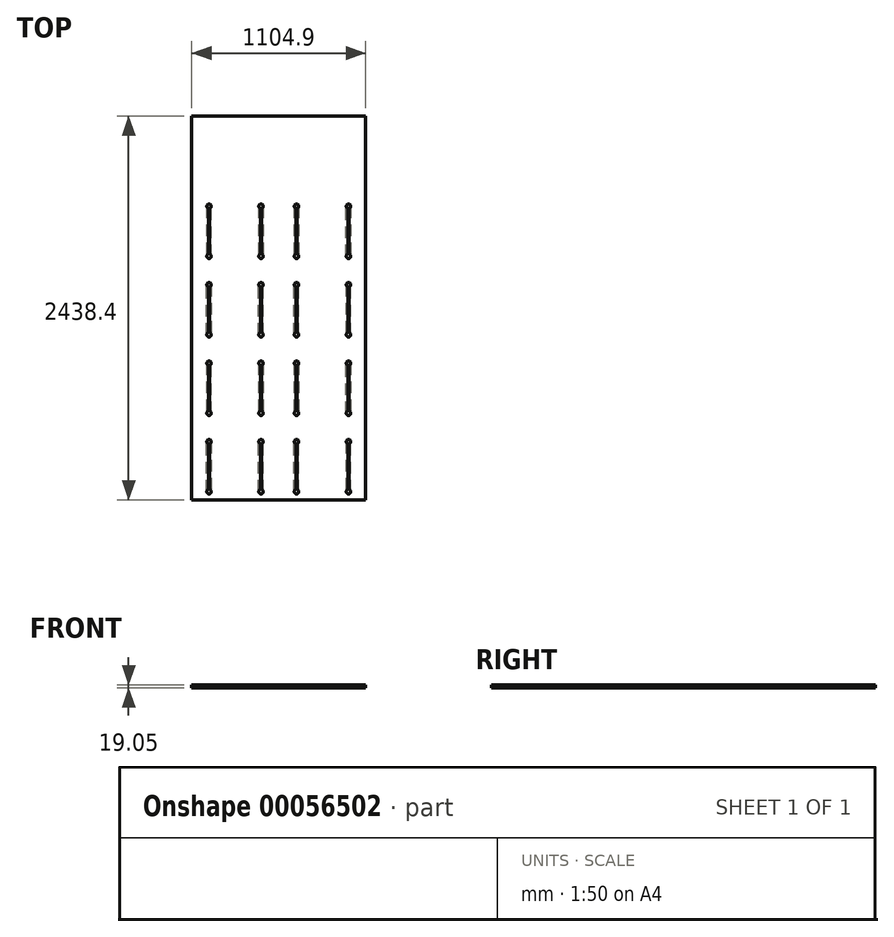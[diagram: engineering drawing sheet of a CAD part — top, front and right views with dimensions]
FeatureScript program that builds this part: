
annotation { "Feature Type Name" : "Feature", "Feature Type Description" : "" }
export const myFeature = defineFeature(function(context is Context, id is Id, definition is map)
    precondition{}
    {
        {
            var Q0;
            Q0=qCreatedBy(makeId("Top.planeOp"),FACE);
            var sketch = newSketch(context, id + "F0", { "sketchPlane" : qUnion([Q0])});
            skLineSegment(sketch, "E0", {"start": v(0, 0) * mm, "end": v(1219.2, 0) * mm, "construction": true});
            skLineSegment(sketch, "E1", {"start": v(1219.2, 0) * mm, "end": v(1219.2, 2438.4) * mm, "construction": true});
            skLineSegment(sketch, "E2", {"start": v(0, 2438.4) * mm, "end": v(1219.2, 2438.4) * mm, "construction": true});
            skLineSegment(sketch, "E3", {"start": v(0, 0) * mm, "end": v(0, 2438.4) * mm, "construction": true});
            skLineSegment(sketch, "E4", {"start": v(609.6, 2700.6) * mm, "end": v(609.6, -302.24) * mm, "construction": true});
            skPoint(sketch, "E4.startSnap0", {"position": v(609.6, 2438.4) * mm});
            skLineSegment(sketch, "E5.bottom", {"start": v(57.15, 0) * mm, "end": v(1162.05, 0) * mm});
            skLineSegment(sketch, "E5.top", {"start": v(57.15, 2438.4) * mm, "end": v(1162.05, 2438.4) * mm});
            skLineSegment(sketch, "E5.left", {"start": v(57.15, 0) * mm, "end": v(57.15, 2438.4) * mm});
            skLineSegment(sketch, "E5.right", {"start": v(1162.05, 0) * mm, "end": v(1162.05, 2438.4) * mm});
            skLineSegment(sketch, "E6.bottom", {"start": v(50.8, 0) * mm, "end": v(88.9, 0) * mm, "construction": true});
            skLineSegment(sketch, "E6.left", {"start": v(50.8, 0) * mm, "end": v(50.8, 2438.4) * mm, "construction": true});
            skLineSegment(sketch, "E6.right", {"start": v(88.9, 0) * mm, "end": v(88.9, 2438.4) * mm, "construction": true});
            skLineSegment(sketch, "E7.bottom", {"start": v(1168.4, 0) * mm, "end": v(1130.3, 0) * mm, "construction": true});
            skLineSegment(sketch, "E7.top", {"start": v(1168.4, 2438.4) * mm, "end": v(1130.3, 2438.4) * mm, "construction": true});
            skLineSegment(sketch, "E7.left", {"start": v(1168.4, 0) * mm, "end": v(1168.4, 2438.4) * mm, "construction": true});
            skLineSegment(sketch, "E7.right", {"start": v(1130.3, 0) * mm, "end": v(1130.3, 2438.4) * mm, "construction": true});
            skLineSegment(sketch, "E8.bottom", {"start": v(88.9, 38.1) * mm, "end": v(1130.3, 38.1) * mm, "construction": true});
            skLineSegment(sketch, "E8.left", {"start": v(88.9, 38.1) * mm, "end": v(88.9, 0) * mm, "construction": true});
            skLineSegment(sketch, "E8.right", {"start": v(1130.3, 38.1) * mm, "end": v(1130.3, 0) * mm, "construction": true});
            skLineSegment(sketch, "E9.bottom", {"start": v(88.9, 2400.3) * mm, "end": v(1130.3, 2400.3) * mm, "construction": true});
            skLineSegment(sketch, "E9.top", {"start": v(88.9, 2438.4) * mm, "end": v(1130.3, 2438.4) * mm, "construction": true});
            skLineSegment(sketch, "E9.left", {"start": v(88.9, 2400.3) * mm, "end": v(88.9, 2438.4) * mm, "construction": true});
            skLineSegment(sketch, "E9.right", {"start": v(1130.3, 2400.3) * mm, "end": v(1130.3, 2438.4) * mm, "construction": true});
            skLineSegment(sketch, "E10", {"start": v(-72.35, 2076.45) * mm, "end": v(1337.6, 2076.45) * mm, "construction": true});
            skLineSegment(sketch, "E11.0.1.0", {"start": v(-72.35, 1733.55) * mm, "end": v(1337.6, 1733.55) * mm, "construction": true});
            skLineSegment(sketch, "E11.0.2.0", {"start": v(-72.35, 1390.65) * mm, "end": v(1337.6, 1390.65) * mm, "construction": true});
            skLineSegment(sketch, "E11.0.3.0", {"start": v(-72.35, 1047.75) * mm, "end": v(1337.6, 1047.75) * mm, "construction": true});
            skLineSegment(sketch, "E11.0.4.0", {"start": v(-72.35, 704.85) * mm, "end": v(1337.6, 704.85) * mm, "construction": true});
            skLineSegment(sketch, "E11.0.5.0", {"start": v(-72.35, 361.95) * mm, "end": v(1337.6, 361.95) * mm, "construction": true});
            skLineSegment(sketch, "E11.direction1", {"start": v(-72.35, 2076.45) * mm, "end": v(-46.95, 2076.45) * mm, "construction": true});
            skLineSegment(sketch, "E11.direction2", {"start": v(-72.35, 2076.45) * mm, "end": v(-72.35, 1733.55) * mm, "construction": true});
            skPoint(sketch, "E12", {"position": v(114.3, 63.5) * mm});
            skPoint(sketch, "E13", {"position": v(609.6, 63.5) * mm});
            skPoint(sketch, "E14.MirrorP", {"position": v(1104.9, 63.5) * mm});
            skPoint(sketch, "E15", {"position": v(361.95, 63.5) * mm});
            skPoint(sketch, "E16", {"position": v(114.3, 279.4) * mm});
            skPoint(sketch, "E17.MirrorP", {"position": v(857.25, 63.5) * mm});
            skPoint(sketch, "E18", {"position": v(361.95, 279.4) * mm});
            skPoint(sketch, "E19", {"position": v(609.6, 279.4) * mm});
            skPoint(sketch, "E20", {"position": v(857.25, 279.4) * mm});
            skPoint(sketch, "E21", {"position": v(1104.9, 279.4) * mm});
            skPoint(sketch, "E22.MirrorP", {"position": v(1104.9, 444.5) * mm});
            skPoint(sketch, "E23.MirrorP", {"position": v(857.25, 444.5) * mm});
            skPoint(sketch, "E24.MirrorP", {"position": v(609.6, 444.5) * mm});
            skPoint(sketch, "E25.MirrorP", {"position": v(361.95, 444.5) * mm});
            skPoint(sketch, "E26.MirrorP", {"position": v(114.3, 444.5) * mm});
            skPoint(sketch, "E27", {"position": v(114.3, 622.3) * mm});
            skPoint(sketch, "E28", {"position": v(361.95, 622.3) * mm});
            skPoint(sketch, "E29", {"position": v(857.25, 622.3) * mm});
            skPoint(sketch, "E30", {"position": v(1104.9, 622.3) * mm});
            skPoint(sketch, "E31", {"position": v(114.3, 965.2) * mm});
            skPoint(sketch, "E32", {"position": v(361.95, 965.2) * mm});
            skPoint(sketch, "E33", {"position": v(857.25, 965.2) * mm});
            skPoint(sketch, "E34", {"position": v(1104.9, 965.2) * mm});
            skPoint(sketch, "E35", {"position": v(609.6, 622.3) * mm});
            skPoint(sketch, "E36.MirrorP", {"position": v(1104.9, 787.4) * mm});
            skPoint(sketch, "E37.MirrorP", {"position": v(857.25, 787.4) * mm});
            skPoint(sketch, "E38.MirrorP", {"position": v(609.6, 787.4) * mm});
            skPoint(sketch, "E39.MirrorP", {"position": v(361.95, 787.4) * mm});
            skPoint(sketch, "E40.MirrorP", {"position": v(114.3, 787.4) * mm});
            skPoint(sketch, "E41", {"position": v(609.6, 965.2) * mm});
            skPoint(sketch, "E42.MirrorP", {"position": v(1104.9, 1130.3) * mm});
            skPoint(sketch, "E43.MirrorP", {"position": v(857.25, 1130.3) * mm});
            skPoint(sketch, "E44.MirrorP", {"position": v(609.6, 1130.3) * mm});
            skPoint(sketch, "E45.MirrorP", {"position": v(361.95, 1130.3) * mm});
            skPoint(sketch, "E46.MirrorP", {"position": v(114.3, 1130.3) * mm});
            skPoint(sketch, "E47.0.1.0", {"position": v(114.3, 1308.1) * mm});
            skPoint(sketch, "E47.0.1.1", {"position": v(361.95, 1308.1) * mm});
            skPoint(sketch, "E47.0.1.2", {"position": v(609.6, 1308.1) * mm});
            skPoint(sketch, "E47.0.1.3", {"position": v(857.25, 1308.1) * mm});
            skPoint(sketch, "E47.0.1.4", {"position": v(1104.9, 1308.1) * mm});
            skPoint(sketch, "E47.0.2.0", {"position": v(114.3, 1651) * mm});
            skPoint(sketch, "E47.0.2.1", {"position": v(361.95, 1651) * mm});
            skPoint(sketch, "E47.0.2.2", {"position": v(609.6, 1651) * mm});
            skPoint(sketch, "E47.0.2.3", {"position": v(857.25, 1651) * mm});
            skPoint(sketch, "E47.0.2.4", {"position": v(1104.9, 1651) * mm});
            skLineSegment(sketch, "E47.direction1", {"start": v(114.3, 965.2) * mm, "end": v(139.7, 965.2) * mm, "construction": true});
            skLineSegment(sketch, "E47.direction2", {"start": v(114.3, 965.2) * mm, "end": v(114.3, 1308.1) * mm, "construction": true});
            skPoint(sketch, "E48.MirrorP", {"position": v(1104.9, 1473.2) * mm});
            skPoint(sketch, "E49.MirrorP", {"position": v(857.25, 1473.2) * mm});
            skPoint(sketch, "E50.MirrorP", {"position": v(609.6, 1473.2) * mm});
            skPoint(sketch, "E51.MirrorP", {"position": v(361.95, 1473.2) * mm});
            skPoint(sketch, "E52.MirrorP", {"position": v(114.3, 1473.2) * mm});
            skPoint(sketch, "E53.MirrorP", {"position": v(1104.9, 1816.1) * mm});
            skPoint(sketch, "E54.MirrorP", {"position": v(857.25, 1816.1) * mm});
            skPoint(sketch, "E55.MirrorP", {"position": v(609.6, 1816.1) * mm});
            skPoint(sketch, "E56.MirrorP", {"position": v(361.95, 1816.1) * mm});
            skPoint(sketch, "E57.MirrorP", {"position": v(114.3, 1816.1) * mm});
            skLineSegment(sketch, "E58", {"start": v(-178.61, 1879.6) * mm, "end": v(1741, 1879.6) * mm, "construction": true});
            skSolve(sketch);
        }
        {
            var Q0;
            Q0 = qSketchRegion(id + "F0", true);
            extrude(context, id + "F1", {"entities" : qUnion([Q0]), "depth" : 19.05 * mm});
        }
        {
            var Q0;
            Q0=qCreatedBy(makeId("Top.planeOp"),FACE);
            var sketch = newSketch(context, id + "F2", { "sketchPlane" : qUnion([Q0])});
            skLineSegment(sketch, "E59.0.0", {"start": v(57.15, 2438.4) * mm, "end": v(57.15, 0) * mm, "construction": true});
            skLineSegment(sketch, "E59.0.1", {"start": v(57.15, 0) * mm, "end": v(1162.05, 0) * mm, "construction": true});
            skLineSegment(sketch, "E59.0.2", {"start": v(1162.05, 0) * mm, "end": v(1162.05, 2438.4) * mm, "construction": true});
            skLineSegment(sketch, "E59.0.3", {"start": v(1162.05, 2438.4) * mm, "end": v(57.15, 2438.4) * mm, "construction": true});
            skArc(sketch, "E60", {"start": v(180.97, 369.89) * mm, "mid": v(166.69, 384.17) * mm, "end": v(152.4, 369.89) * mm});
            skArc(sketch, "E61", {"start": v(152.4, 52.39) * mm, "mid": v(166.69, 38.1) * mm, "end": v(180.97, 52.39) * mm});
            skLineSegment(sketch, "E62", {"start": v(152.4, 52.39) * mm, "end": v(152.4, 369.89) * mm});
            skLineSegment(sketch, "E63", {"start": v(180.97, 369.89) * mm, "end": v(180.98, 52.39) * mm});
            skLineSegment(sketch, "E64.MirrorCS", {"start": v(1038.22, 369.89) * mm, "end": v(1038.22, 52.39) * mm});
            skLineSegment(sketch, "E65.MirrorCS", {"start": v(1066.8, 52.39) * mm, "end": v(1066.8, 369.89) * mm});
            skArc(sketch, "E66.MirrorCS", {"start": v(1038.22, 369.89) * mm, "mid": v(1052.51, 384.17) * mm, "end": v(1066.8, 369.89) * mm});
            skArc(sketch, "E67.MirrorCS", {"start": v(1066.8, 52.39) * mm, "mid": v(1052.51, 38.1) * mm, "end": v(1038.22, 52.39) * mm});
            skArc(sketch, "E68", {"start": v(482.6, 52.39) * mm, "mid": v(496.89, 38.1) * mm, "end": v(511.18, 52.39) * mm});
            skArc(sketch, "E69", {"start": v(511.18, 369.89) * mm, "mid": v(496.89, 384.18) * mm, "end": v(482.6, 369.89) * mm});
            skLineSegment(sketch, "E70", {"start": v(511.18, 52.39) * mm, "end": v(511.18, 369.89) * mm});
            skLineSegment(sketch, "E71", {"start": v(482.6, 52.39) * mm, "end": v(482.6, 369.89) * mm});
            skArc(sketch, "E72.MirrorCS", {"start": v(708.02, 369.89) * mm, "mid": v(722.31, 384.18) * mm, "end": v(736.6, 369.89) * mm});
            skLineSegment(sketch, "E73.MirrorCS", {"start": v(708.02, 52.39) * mm, "end": v(708.02, 369.89) * mm});
            skLineSegment(sketch, "E74.MirrorCS", {"start": v(736.6, 52.39) * mm, "end": v(736.6, 369.89) * mm});
            skArc(sketch, "E75.MirrorCS", {"start": v(736.6, 52.39) * mm, "mid": v(722.31, 38.1) * mm, "end": v(708.02, 52.39) * mm});
            skLineSegment(sketch, "E76", {"start": v(-152.27, 1879.6) * mm, "end": v(1461.57, 1879.6) * mm, "construction": true});
            skLineSegment(sketch, "E77", {"start": v(-432.69, 958.85) * mm, "end": v(1846.95, 958.85) * mm, "construction": true});
            skLineSegment(sketch, "E78", {"start": v(-90.79, 460.37) * mm, "end": v(1462.9, 460.37) * mm, "construction": true});
            skArc(sketch, "E79.MirrorCS", {"start": v(180.97, 550.86) * mm, "mid": v(166.69, 536.57) * mm, "end": v(152.4, 550.86) * mm});
            skLineSegment(sketch, "E80.MirrorCS", {"start": v(152.4, 868.36) * mm, "end": v(152.4, 550.86) * mm});
            skLineSegment(sketch, "E81.MirrorCS", {"start": v(180.97, 550.86) * mm, "end": v(180.97, 868.36) * mm});
            skArc(sketch, "E82.MirrorCS", {"start": v(152.4, 868.36) * mm, "mid": v(166.69, 882.65) * mm, "end": v(180.97, 868.36) * mm});
            skArc(sketch, "E83.MirrorCS", {"start": v(152.4, 1049.34) * mm, "mid": v(166.69, 1035.05) * mm, "end": v(180.97, 1049.34) * mm});
            skLineSegment(sketch, "E84.MirrorCS", {"start": v(180.97, 1366.84) * mm, "end": v(180.97, 1049.34) * mm});
            skLineSegment(sketch, "E85.MirrorCS", {"start": v(152.4, 1049.34) * mm, "end": v(152.4, 1366.84) * mm});
            skArc(sketch, "E86.MirrorCS", {"start": v(180.97, 1366.84) * mm, "mid": v(166.69, 1381.12) * mm, "end": v(152.4, 1366.84) * mm});
            skArc(sketch, "E87.MirrorCS", {"start": v(180.97, 1547.81) * mm, "mid": v(166.69, 1533.53) * mm, "end": v(152.4, 1547.81) * mm});
            skLineSegment(sketch, "E88.MirrorCS", {"start": v(152.4, 1865.31) * mm, "end": v(152.4, 1547.81) * mm});
            skLineSegment(sketch, "E89.MirrorCS", {"start": v(180.97, 1547.81) * mm, "end": v(180.98, 1865.31) * mm});
            skArc(sketch, "E90.MirrorCS", {"start": v(152.4, 1865.31) * mm, "mid": v(166.69, 1879.6) * mm, "end": v(180.97, 1865.31) * mm});
            skArc(sketch, "E91.MirrorCS", {"start": v(482.6, 1865.31) * mm, "mid": v(496.89, 1879.6) * mm, "end": v(511.18, 1865.31) * mm});
            skLineSegment(sketch, "E92.MirrorCS", {"start": v(482.6, 1865.31) * mm, "end": v(482.6, 1547.81) * mm});
            skArc(sketch, "E93.MirrorCS", {"start": v(1038.22, 550.86) * mm, "mid": v(1052.51, 536.57) * mm, "end": v(1066.8, 550.86) * mm});
            skLineSegment(sketch, "E94.MirrorCS", {"start": v(1066.8, 868.36) * mm, "end": v(1066.8, 550.86) * mm});
            skLineSegment(sketch, "E95.MirrorCS", {"start": v(1038.22, 550.86) * mm, "end": v(1038.22, 868.36) * mm});
            skArc(sketch, "E96.MirrorCS", {"start": v(1066.8, 868.36) * mm, "mid": v(1052.51, 882.65) * mm, "end": v(1038.22, 868.36) * mm});
            skArc(sketch, "E97.MirrorCS", {"start": v(708.02, 550.86) * mm, "mid": v(722.31, 536.57) * mm, "end": v(736.6, 550.86) * mm});
            skArc(sketch, "E98.MirrorCS", {"start": v(736.6, 868.36) * mm, "mid": v(722.31, 882.65) * mm, "end": v(708.02, 868.36) * mm});
            skLineSegment(sketch, "E99.MirrorCS", {"start": v(708.02, 868.36) * mm, "end": v(708.02, 550.86) * mm});
            skLineSegment(sketch, "E100.MirrorCS", {"start": v(736.6, 868.36) * mm, "end": v(736.6, 550.86) * mm});
            skArc(sketch, "E101.MirrorCS", {"start": v(511.18, 550.86) * mm, "mid": v(496.89, 536.57) * mm, "end": v(482.6, 550.86) * mm});
            skLineSegment(sketch, "E102.MirrorCS", {"start": v(482.6, 868.36) * mm, "end": v(482.6, 550.86) * mm});
            skLineSegment(sketch, "E103.MirrorCS", {"start": v(511.18, 868.36) * mm, "end": v(511.18, 550.86) * mm});
            skArc(sketch, "E104.MirrorCS", {"start": v(482.6, 868.36) * mm, "mid": v(496.89, 882.65) * mm, "end": v(511.18, 868.36) * mm});
            skLineSegment(sketch, "E105.MirrorCS", {"start": v(-432.69, -38.1) * mm, "end": v(1846.95, -38.1) * mm, "construction": true});
            skArc(sketch, "E106.MirrorCS", {"start": v(736.6, 1049.34) * mm, "mid": v(722.31, 1035.05) * mm, "end": v(708.02, 1049.34) * mm});
            skArc(sketch, "E107.MirrorCS", {"start": v(708.02, 1547.81) * mm, "mid": v(722.31, 1533.53) * mm, "end": v(736.6, 1547.81) * mm});
            skLineSegment(sketch, "E108.MirrorCS", {"start": v(708.02, 1049.34) * mm, "end": v(708.02, 1366.84) * mm});
            skArc(sketch, "E109.MirrorCS", {"start": v(1038.22, 1547.81) * mm, "mid": v(1052.51, 1533.53) * mm, "end": v(1066.8, 1547.81) * mm});
            skArc(sketch, "E110.MirrorCS", {"start": v(1066.8, 1049.34) * mm, "mid": v(1052.51, 1035.05) * mm, "end": v(1038.22, 1049.34) * mm});
            skArc(sketch, "E111.MirrorCS", {"start": v(1038.22, 1366.84) * mm, "mid": v(1052.51, 1381.12) * mm, "end": v(1066.8, 1366.84) * mm});
            skArc(sketch, "E112.MirrorCS", {"start": v(1066.8, 1865.31) * mm, "mid": v(1052.51, 1879.6) * mm, "end": v(1038.22, 1865.31) * mm});
            skArc(sketch, "E113.MirrorCS", {"start": v(736.6, 1865.31) * mm, "mid": v(722.31, 1879.6) * mm, "end": v(708.02, 1865.31) * mm});
            skLineSegment(sketch, "E114.MirrorCS", {"start": v(708.02, 1865.31) * mm, "end": v(708.02, 1547.81) * mm});
            skLineSegment(sketch, "E115.MirrorCS", {"start": v(1066.8, 1049.34) * mm, "end": v(1066.8, 1366.84) * mm});
            skLineSegment(sketch, "E116.MirrorCS", {"start": v(1066.8, 1865.31) * mm, "end": v(1066.8, 1547.81) * mm});
            skArc(sketch, "E117.MirrorCS", {"start": v(708.02, 1366.84) * mm, "mid": v(722.31, 1381.13) * mm, "end": v(736.6, 1366.84) * mm});
            skLineSegment(sketch, "E118.MirrorCS", {"start": v(736.6, 1049.34) * mm, "end": v(736.6, 1366.84) * mm});
            skLineSegment(sketch, "E119.MirrorCS", {"start": v(1038.22, 1366.84) * mm, "end": v(1038.22, 1049.34) * mm});
            skLineSegment(sketch, "E120.MirrorCS", {"start": v(1038.22, 1547.81) * mm, "end": v(1038.22, 1865.31) * mm});
            skLineSegment(sketch, "E121.MirrorCS", {"start": v(736.6, 1865.31) * mm, "end": v(736.6, 1547.81) * mm});
            skArc(sketch, "E122.MirrorCS", {"start": v(511.18, 1547.81) * mm, "mid": v(496.89, 1533.53) * mm, "end": v(482.6, 1547.81) * mm});
            skArc(sketch, "E123.MirrorCS", {"start": v(511.18, 1366.84) * mm, "mid": v(496.89, 1381.13) * mm, "end": v(482.6, 1366.84) * mm});
            skLineSegment(sketch, "E124.MirrorCS", {"start": v(482.6, 1049.34) * mm, "end": v(482.6, 1366.84) * mm});
            skLineSegment(sketch, "E125.MirrorCS", {"start": v(511.18, 1049.34) * mm, "end": v(511.18, 1366.84) * mm});
            skLineSegment(sketch, "E126.MirrorCS", {"start": v(511.18, 1865.31) * mm, "end": v(511.18, 1547.81) * mm});
            skArc(sketch, "E127.MirrorCS", {"start": v(482.6, 1049.34) * mm, "mid": v(496.89, 1035.05) * mm, "end": v(511.18, 1049.34) * mm});
            skSolve(sketch);
        }
        {
            var Q0;
            Q0 = qSketchRegion(id + "F2", true);
            extrude(context, id + "F3", {"entities" : qUnion([Q0]), "operationType" : NewBodyOperationType.REMOVE, "depth" : 3.17 * mm});
        }
        {
            var Q0;
            Q0=qCreatedBy(makeId("Top.planeOp"),FACE);
            var sketch = newSketch(context, id + "F4", { "sketchPlane" : qUnion([Q0])});
            skArc(sketch, "E128", {"start": v(1048.07, 65.97) * mm, "mid": v(1052.51, 38.1) * mm, "end": v(1056.96, 65.97) * mm});
            skArc(sketch, "E129", {"start": v(1056.96, 356.3) * mm, "mid": v(1052.51, 384.17) * mm, "end": v(1048.07, 356.3) * mm});
            skLineSegment(sketch, "E130", {"start": v(1048.07, 65.97) * mm, "end": v(1048.07, 356.3) * mm});
            skLineSegment(sketch, "E131", {"start": v(1056.96, 65.97) * mm, "end": v(1056.96, 356.3) * mm});
            skLineSegment(sketch, "E132", {"start": v(1052.51, 52.39) * mm, "end": v(1052.51, 369.89) * mm, "construction": true});
            skPoint(sketch, "E133", {"position": v(722.31, 369.89) * mm});
            skArc(sketch, "E134.1.0.0", {"start": v(726.76, 356.3) * mm, "mid": v(722.31, 384.17) * mm, "end": v(717.87, 356.3) * mm});
            skLineSegment(sketch, "E134.1.0.1", {"start": v(726.76, 65.97) * mm, "end": v(726.76, 356.3) * mm});
            skLineSegment(sketch, "E134.1.0.2", {"start": v(717.87, 65.97) * mm, "end": v(717.87, 356.3) * mm});
            skArc(sketch, "E134.1.0.3", {"start": v(717.87, 65.97) * mm, "mid": v(722.31, 38.1) * mm, "end": v(726.76, 65.97) * mm});
            skLineSegment(sketch, "E134.direction1", {"start": v(1048.07, 356.3) * mm, "end": v(717.87, 356.3) * mm, "construction": true});
            skPoint(sketch, "E135", {"position": v(496.89, 369.89) * mm});
            skArc(sketch, "E136.1.0.0", {"start": v(501.33, 356.3) * mm, "mid": v(496.89, 384.17) * mm, "end": v(492.44, 356.3) * mm});
            skLineSegment(sketch, "E136.1.0.1", {"start": v(501.33, 65.97) * mm, "end": v(501.33, 356.3) * mm});
            skLineSegment(sketch, "E136.1.0.2", {"start": v(492.44, 65.97) * mm, "end": v(492.44, 356.3) * mm});
            skArc(sketch, "E136.1.0.3", {"start": v(492.44, 65.97) * mm, "mid": v(496.89, 38.1) * mm, "end": v(501.33, 65.97) * mm});
            skLineSegment(sketch, "E136.direction1", {"start": v(717.87, 356.3) * mm, "end": v(492.44, 356.3) * mm, "construction": true});
            skArc(sketch, "E137.1.0.0", {"start": v(171.13, 356.3) * mm, "mid": v(166.69, 384.17) * mm, "end": v(162.24, 356.3) * mm});
            skLineSegment(sketch, "E137.1.0.1", {"start": v(171.13, 65.97) * mm, "end": v(171.13, 356.3) * mm});
            skLineSegment(sketch, "E137.1.0.2", {"start": v(162.24, 65.97) * mm, "end": v(162.24, 356.3) * mm});
            skArc(sketch, "E137.1.0.3", {"start": v(162.24, 65.97) * mm, "mid": v(166.69, 38.1) * mm, "end": v(171.13, 65.97) * mm});
            skLineSegment(sketch, "E137.direction1", {"start": v(492.44, 356.3) * mm, "end": v(162.24, 356.3) * mm, "construction": true});
            skPoint(sketch, "E138", {"position": v(1052.51, 550.86) * mm});
            skLineSegment(sketch, "E139.0.1.0", {"start": v(717.87, 854.78) * mm, "end": v(492.44, 854.78) * mm, "construction": true});
            skLineSegment(sketch, "E139.0.1.1", {"start": v(1048.07, 854.78) * mm, "end": v(717.87, 854.78) * mm, "construction": true});
            skArc(sketch, "E139.0.1.2", {"start": v(501.33, 854.78) * mm, "mid": v(496.89, 882.65) * mm, "end": v(492.44, 854.78) * mm});
            skLineSegment(sketch, "E139.0.1.3", {"start": v(501.33, 564.44) * mm, "end": v(501.33, 854.78) * mm});
            skArc(sketch, "E139.0.1.4", {"start": v(717.87, 564.44) * mm, "mid": v(722.31, 536.58) * mm, "end": v(726.76, 564.44) * mm});
            skArc(sketch, "E139.0.1.5", {"start": v(171.13, 854.78) * mm, "mid": v(166.69, 882.65) * mm, "end": v(162.24, 854.78) * mm});
            skLineSegment(sketch, "E139.0.1.6", {"start": v(492.44, 564.44) * mm, "end": v(492.44, 854.78) * mm});
            skArc(sketch, "E139.0.1.7", {"start": v(1048.07, 564.44) * mm, "mid": v(1052.51, 536.58) * mm, "end": v(1056.96, 564.44) * mm});
            skArc(sketch, "E139.0.1.8", {"start": v(1056.96, 854.78) * mm, "mid": v(1052.51, 882.65) * mm, "end": v(1048.07, 854.78) * mm});
            skLineSegment(sketch, "E139.0.1.9", {"start": v(1048.07, 564.44) * mm, "end": v(1048.07, 854.78) * mm});
            skLineSegment(sketch, "E139.0.1.10", {"start": v(1056.96, 564.44) * mm, "end": v(1056.96, 854.78) * mm});
            skLineSegment(sketch, "E139.0.1.11", {"start": v(726.76, 564.44) * mm, "end": v(726.76, 854.78) * mm});
            skLineSegment(sketch, "E139.0.1.12", {"start": v(717.87, 564.44) * mm, "end": v(717.87, 854.78) * mm});
            skArc(sketch, "E139.0.1.13", {"start": v(492.44, 564.44) * mm, "mid": v(496.89, 536.58) * mm, "end": v(501.33, 564.44) * mm});
            skArc(sketch, "E139.0.1.14", {"start": v(162.24, 564.44) * mm, "mid": v(166.69, 536.58) * mm, "end": v(171.13, 564.44) * mm});
            skLineSegment(sketch, "E139.0.1.15", {"start": v(171.13, 564.44) * mm, "end": v(171.13, 854.78) * mm});
            skLineSegment(sketch, "E139.0.1.16", {"start": v(492.44, 854.78) * mm, "end": v(162.24, 854.78) * mm, "construction": true});
            skPoint(sketch, "E139.0.1.17", {"position": v(722.31, 868.36) * mm});
            skLineSegment(sketch, "E139.0.1.18", {"start": v(162.24, 564.44) * mm, "end": v(162.24, 854.78) * mm});
            skPoint(sketch, "E139.0.1.19", {"position": v(496.89, 868.36) * mm});
            skLineSegment(sketch, "E139.0.1.20", {"start": v(1052.51, 550.86) * mm, "end": v(1052.51, 868.36) * mm, "construction": true});
            skArc(sketch, "E139.0.1.21", {"start": v(726.76, 854.78) * mm, "mid": v(722.31, 882.65) * mm, "end": v(717.87, 854.78) * mm});
            skLineSegment(sketch, "E139.0.2.0", {"start": v(717.87, 1353.26) * mm, "end": v(492.44, 1353.26) * mm, "construction": true});
            skLineSegment(sketch, "E139.0.2.1", {"start": v(1048.07, 1353.26) * mm, "end": v(717.87, 1353.26) * mm, "construction": true});
            skArc(sketch, "E139.0.2.2", {"start": v(501.33, 1353.26) * mm, "mid": v(496.89, 1381.12) * mm, "end": v(492.44, 1353.26) * mm});
            skLineSegment(sketch, "E139.0.2.3", {"start": v(501.33, 1062.92) * mm, "end": v(501.33, 1353.26) * mm});
            skArc(sketch, "E139.0.2.4", {"start": v(717.87, 1062.92) * mm, "mid": v(722.31, 1035.05) * mm, "end": v(726.76, 1062.92) * mm});
            skArc(sketch, "E139.0.2.5", {"start": v(171.13, 1353.26) * mm, "mid": v(166.69, 1381.12) * mm, "end": v(162.24, 1353.26) * mm});
            skLineSegment(sketch, "E139.0.2.6", {"start": v(492.44, 1062.92) * mm, "end": v(492.44, 1353.26) * mm});
            skArc(sketch, "E139.0.2.7", {"start": v(1048.07, 1062.92) * mm, "mid": v(1052.51, 1035.05) * mm, "end": v(1056.96, 1062.92) * mm});
            skArc(sketch, "E139.0.2.8", {"start": v(1056.96, 1353.26) * mm, "mid": v(1052.51, 1381.12) * mm, "end": v(1048.07, 1353.26) * mm});
            skLineSegment(sketch, "E139.0.2.9", {"start": v(1048.07, 1062.92) * mm, "end": v(1048.07, 1353.26) * mm});
            skLineSegment(sketch, "E139.0.2.10", {"start": v(1056.96, 1062.92) * mm, "end": v(1056.96, 1353.26) * mm});
            skLineSegment(sketch, "E139.0.2.11", {"start": v(726.76, 1062.92) * mm, "end": v(726.76, 1353.26) * mm});
            skLineSegment(sketch, "E139.0.2.12", {"start": v(717.87, 1062.92) * mm, "end": v(717.87, 1353.26) * mm});
            skArc(sketch, "E139.0.2.13", {"start": v(492.44, 1062.92) * mm, "mid": v(496.89, 1035.05) * mm, "end": v(501.33, 1062.92) * mm});
            skArc(sketch, "E139.0.2.14", {"start": v(162.24, 1062.92) * mm, "mid": v(166.69, 1035.05) * mm, "end": v(171.13, 1062.92) * mm});
            skLineSegment(sketch, "E139.0.2.15", {"start": v(171.13, 1062.92) * mm, "end": v(171.13, 1353.26) * mm});
            skLineSegment(sketch, "E139.0.2.16", {"start": v(492.44, 1353.26) * mm, "end": v(162.24, 1353.26) * mm, "construction": true});
            skPoint(sketch, "E139.0.2.17", {"position": v(722.31, 1366.84) * mm});
            skLineSegment(sketch, "E139.0.2.18", {"start": v(162.24, 1062.92) * mm, "end": v(162.24, 1353.26) * mm});
            skPoint(sketch, "E139.0.2.19", {"position": v(496.89, 1366.84) * mm});
            skLineSegment(sketch, "E139.0.2.20", {"start": v(1052.51, 1049.34) * mm, "end": v(1052.51, 1366.84) * mm, "construction": true});
            skArc(sketch, "E139.0.2.21", {"start": v(726.76, 1353.26) * mm, "mid": v(722.31, 1381.12) * mm, "end": v(717.87, 1353.26) * mm});
            skLineSegment(sketch, "E139.0.3.0", {"start": v(717.87, 1851.73) * mm, "end": v(492.44, 1851.73) * mm, "construction": true});
            skLineSegment(sketch, "E139.0.3.1", {"start": v(1048.07, 1851.73) * mm, "end": v(717.87, 1851.73) * mm, "construction": true});
            skArc(sketch, "E139.0.3.2", {"start": v(501.33, 1851.73) * mm, "mid": v(496.89, 1879.6) * mm, "end": v(492.44, 1851.73) * mm});
            skLineSegment(sketch, "E139.0.3.3", {"start": v(501.33, 1561.4) * mm, "end": v(501.33, 1851.73) * mm});
            skArc(sketch, "E139.0.3.4", {"start": v(717.87, 1561.4) * mm, "mid": v(722.31, 1533.53) * mm, "end": v(726.76, 1561.4) * mm});
            skArc(sketch, "E139.0.3.5", {"start": v(171.13, 1851.73) * mm, "mid": v(166.69, 1879.6) * mm, "end": v(162.24, 1851.73) * mm});
            skLineSegment(sketch, "E139.0.3.6", {"start": v(492.44, 1561.4) * mm, "end": v(492.44, 1851.73) * mm});
            skArc(sketch, "E139.0.3.7", {"start": v(1048.07, 1561.4) * mm, "mid": v(1052.51, 1533.53) * mm, "end": v(1056.96, 1561.4) * mm});
            skArc(sketch, "E139.0.3.8", {"start": v(1056.96, 1851.73) * mm, "mid": v(1052.51, 1879.6) * mm, "end": v(1048.07, 1851.73) * mm});
            skLineSegment(sketch, "E139.0.3.9", {"start": v(1048.07, 1561.4) * mm, "end": v(1048.07, 1851.73) * mm});
            skLineSegment(sketch, "E139.0.3.10", {"start": v(1056.96, 1561.4) * mm, "end": v(1056.96, 1851.73) * mm});
            skLineSegment(sketch, "E139.0.3.11", {"start": v(726.76, 1561.4) * mm, "end": v(726.76, 1851.73) * mm});
            skLineSegment(sketch, "E139.0.3.12", {"start": v(717.87, 1561.4) * mm, "end": v(717.87, 1851.73) * mm});
            skArc(sketch, "E139.0.3.13", {"start": v(492.44, 1561.4) * mm, "mid": v(496.89, 1533.53) * mm, "end": v(501.33, 1561.4) * mm});
            skArc(sketch, "E139.0.3.14", {"start": v(162.24, 1561.4) * mm, "mid": v(166.69, 1533.53) * mm, "end": v(171.13, 1561.4) * mm});
            skLineSegment(sketch, "E139.0.3.15", {"start": v(171.13, 1561.4) * mm, "end": v(171.13, 1851.73) * mm});
            skLineSegment(sketch, "E139.0.3.16", {"start": v(492.44, 1851.73) * mm, "end": v(162.24, 1851.73) * mm, "construction": true});
            skPoint(sketch, "E139.0.3.17", {"position": v(722.31, 1865.31) * mm});
            skLineSegment(sketch, "E139.0.3.18", {"start": v(162.24, 1561.4) * mm, "end": v(162.24, 1851.73) * mm});
            skPoint(sketch, "E139.0.3.19", {"position": v(496.89, 1865.31) * mm});
            skLineSegment(sketch, "E139.0.3.20", {"start": v(1052.51, 1547.81) * mm, "end": v(1052.51, 1865.31) * mm, "construction": true});
            skArc(sketch, "E139.0.3.21", {"start": v(726.76, 1851.73) * mm, "mid": v(722.31, 1879.6) * mm, "end": v(717.87, 1851.73) * mm});
            skLineSegment(sketch, "E139.direction1", {"start": v(492.44, 356.3) * mm, "end": v(517.84, 356.3) * mm, "construction": true});
            skLineSegment(sketch, "E139.direction2", {"start": v(492.44, 356.3) * mm, "end": v(492.44, 854.78) * mm, "construction": true});
            skSolve(sketch);
        }
        {
            var Q0;
            Q0 = qSketchRegion(id + "F4", true);
            extrude(context, id + "F5", {"entities" : qUnion([Q0]), "operationType" : NewBodyOperationType.REMOVE, "depth" : 25.4 * mm});
        }
    });
